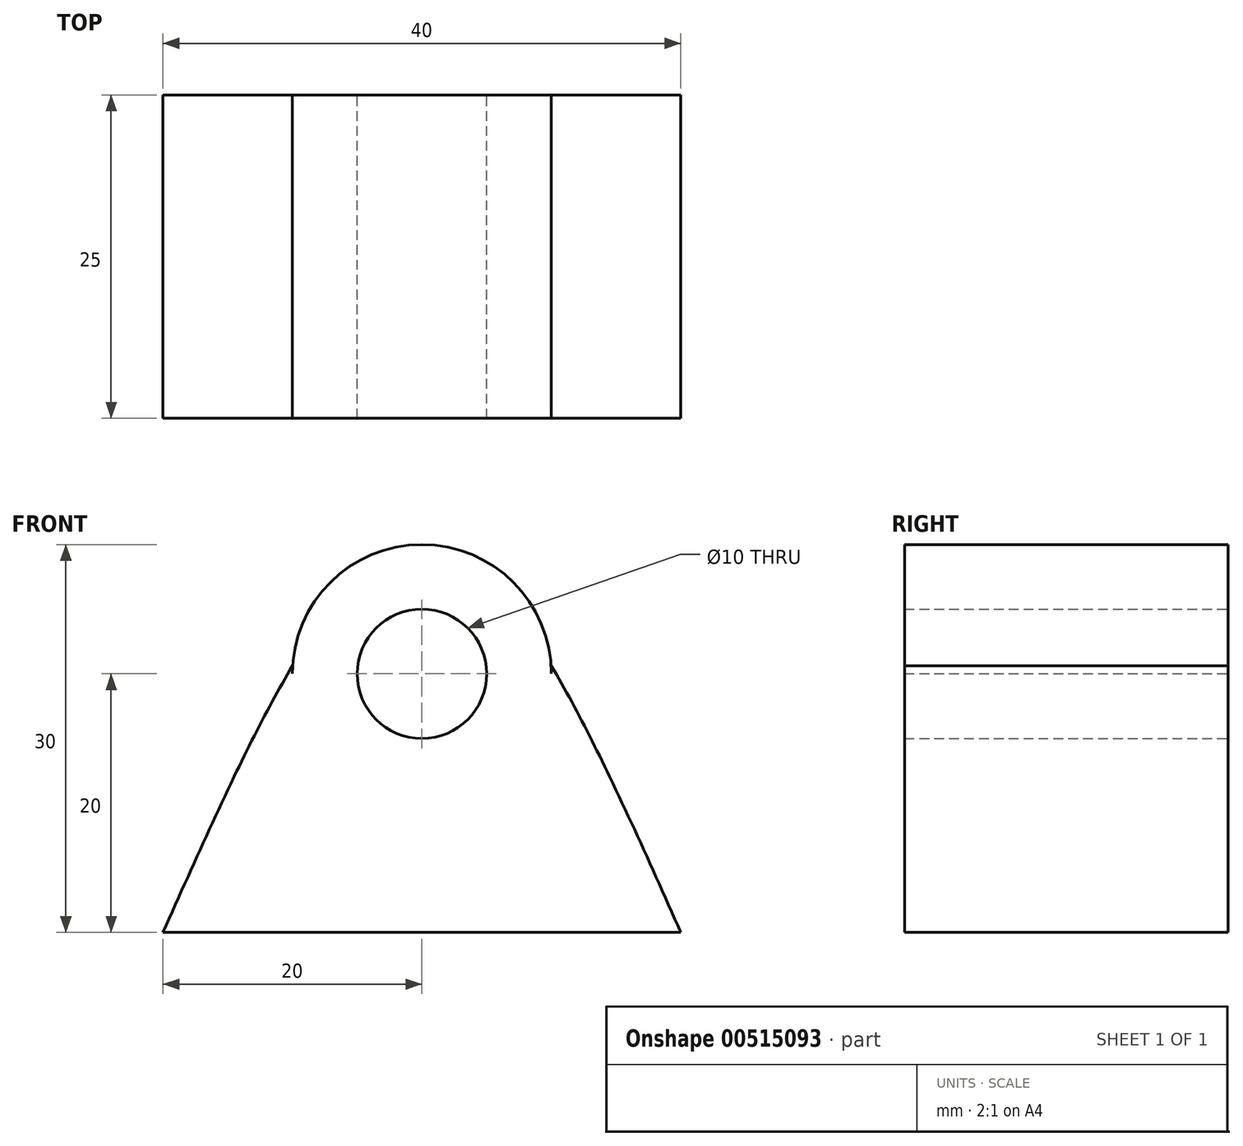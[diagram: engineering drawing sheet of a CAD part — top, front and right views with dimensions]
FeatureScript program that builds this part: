
annotation { "Feature Type Name" : "Feature", "Feature Type Description" : "" }
export const myFeature = defineFeature(function(context is Context, id is Id, definition is map)
    precondition{}
    {
        {
            var Q0;
            Q0=qCreatedBy(makeId("Front.planeOp"),FACE);
            var sketch = newSketch(context, id + "F0", { "sketchPlane" : qUnion([Q0])});
            skCircle(sketch, "E0", {"center": v(0, 20) * mm, "radius": 5 * mm});
            skSolve(sketch);
        }
        {
            var Q0;
            Q0=qCreatedBy(makeId("Front.planeOp"),FACE);
            var sketch = newSketch(context, id + "F1", { "sketchPlane" : qUnion([Q0])});
            skLineSegment(sketch, "E1.bottom", {"start": v(10, 0) * mm, "end": v(-10, 0) * mm});
            skLineSegment(sketch, "E1.top", {"start": v(10, 30) * mm, "end": v(-10, 30) * mm});
            skLineSegment(sketch, "E1.left", {"start": v(10, 0) * mm, "end": v(10, 30) * mm});
            skLineSegment(sketch, "E1.right", {"start": v(-10, 0) * mm, "end": v(-10, 30) * mm});
            skCircle(sketch, "E2", {"center": v(0, 20) * mm, "radius": 10 * mm});
            skLineSegment(sketch, "E3.bottom", {"start": v(-20, 12.04) * mm, "end": v(20, 12.04) * mm});
            skLineSegment(sketch, "E3.top", {"start": v(-20, 0) * mm, "end": v(20, 0) * mm});
            skLineSegment(sketch, "E3.left", {"start": v(-20, 12.04) * mm, "end": v(-20, 0) * mm});
            skLineSegment(sketch, "E3.right", {"start": v(20, 12.04) * mm, "end": v(20, 0) * mm});
            skFitSpline(sketch, "E4", {"points": [v(-20, 0) * mm, v(0, 30) * mm, v(20, 0) * mm], "startDerivative": vector(40, 90) * mm, "endDerivative": vector(40, -90) * mm});
            skSolve(sketch);
        }
        {
            var Q0;
            {var subQ0=sQuery(id+"F1.wireOp",EDGE,"E2");var subQ1=makeQuery(id+"F1.imprint","INTERSECT",VERTEX,{"derivedFrom":[sQuery(id+"F1.wireOp",EDGE,"E1.left"),subQ0]});Q0=makeQuery(id+"F1.imprint","IMPRINT",FACE,{"disambiguationData":[TD([[makeQuery(id+"F1.imprint","IMPRINT",EDGE,{"disambiguationData":[TD([[subQ1,-1.0]])],"derivedFrom":subQ0}),1.0]])]});}
            var Q1;
            {var subQ0=sQuery(id+"F1.wireOp",EDGE,"E3.bottom");var subQ1=sQuery(id+"F1.wireOp",EDGE,"E1.right");var subQ2=makeQuery(id+"F1.imprint","INTERSECT",VERTEX,{"derivedFrom":[subQ1,subQ0]});Q1=makeQuery(id+"F1.imprint","IMPRINT",FACE,{"disambiguationData":[TD([[makeQuery(id+"F1.imprint","IMPRINT",EDGE,{"disambiguationData":[TD([[subQ2,-1.0]])],"derivedFrom":subQ1}),-1.0]])]});}
            var Q2;
            {var subQ0=sQuery(id+"F1.wireOp",EDGE,"E3.bottom");var subQ1=sQuery(id+"F1.wireOp",EDGE,"E1.right");var subQ2=makeQuery(id+"F1.imprint","INTERSECT",VERTEX,{"derivedFrom":[subQ1,subQ0]});Q2=makeQuery(id+"F1.imprint","IMPRINT",FACE,{"disambiguationData":[TD([[makeQuery(id+"F1.imprint","IMPRINT",EDGE,{"disambiguationData":[TD([[subQ2,-1.0]])],"derivedFrom":subQ1}),1.0]])]});}
            var Q3;
            {var subQ0=sQuery(id+"F1.wireOp",EDGE,"E3.top");var subQ1=sQuery(id+"F1.wireOp",EDGE,"E1.right");var subQ2=makeQuery(id+"F1.imprint","INTERSECT",VERTEX,{"derivedFrom":[subQ1,subQ0]});Q3=makeQuery(id+"F1.imprint","IMPRINT",FACE,{"disambiguationData":[TD([[makeQuery(id+"F1.imprint","IMPRINT",EDGE,{"disambiguationData":[TD([[subQ2,-1.0]])],"derivedFrom":subQ1}),1.0]])]});}
            var Q4;
            {var subQ6=sQuery(id+"F1.wireOp",EDGE,"E3.top");var subQ8=sQuery(id+"F1.wireOp",EDGE,"E1.left");var subQ9=makeQuery(id+"F1.imprint","INTERSECT",VERTEX,{"derivedFrom":[subQ8,subQ6]});Q4=makeQuery(id+"F1.imprint","IMPRINT",FACE,{"disambiguationData":[TD([[makeQuery(id+"F1.imprint","IMPRINT",EDGE,{"disambiguationData":[TD([[subQ9,-1.0]])],"derivedFrom":subQ8}),1.0]])]});}
            var Q5;
            {var subQ0=sQuery(id+"F1.wireOp",EDGE,"E3.bottom");var subQ1=sQuery(id+"F1.wireOp",EDGE,"E1.left");var subQ2=makeQuery(id+"F1.imprint","INTERSECT",VERTEX,{"derivedFrom":[subQ1,subQ0]});Q5=makeQuery(id+"F1.imprint","IMPRINT",FACE,{"disambiguationData":[TD([[makeQuery(id+"F1.imprint","IMPRINT",EDGE,{"disambiguationData":[TD([[subQ2,-1.0]])],"derivedFrom":subQ1}),1.0]])]});}
            var Q6;
            {var subQ0=sQuery(id+"F1.wireOp",EDGE,"E3.bottom");var subQ1=sQuery(id+"F1.wireOp",EDGE,"E2");var subQ2=makeQuery(id+"F1.imprint","INTERSECT",VERTEX,{"disambiguationData":[OD(0.0)],"derivedFrom":[subQ1,subQ0]});Q6=makeQuery(id+"F1.imprint","IMPRINT",FACE,{"disambiguationData":[TD([[makeQuery(id+"F1.imprint","IMPRINT",EDGE,{"disambiguationData":[TD([[subQ2,-1.0]])],"derivedFrom":subQ1}),1.0]])]});}
            var Q7;
            {var subQ0=sQuery(id+"F1.wireOp",EDGE,"E3.bottom");var subQ1=sQuery(id+"F1.wireOp",EDGE,"E1.left");var subQ2=makeQuery(id+"F1.imprint","INTERSECT",VERTEX,{"derivedFrom":[subQ1,subQ0]});Q7=makeQuery(id+"F1.imprint","IMPRINT",FACE,{"disambiguationData":[TD([[makeQuery(id+"F1.imprint","IMPRINT",EDGE,{"disambiguationData":[TD([[subQ2,-1.0]])],"derivedFrom":subQ1}),-1.0]])]});}
            var Q8;
            {var subQ0=sQuery(id+"F1.wireOp",EDGE,"E3.top");var subQ1=sQuery(id+"F1.wireOp",EDGE,"E1.left");var subQ2=makeQuery(id+"F1.imprint","INTERSECT",VERTEX,{"derivedFrom":[subQ1,subQ0]});Q8=makeQuery(id+"F1.imprint","IMPRINT",FACE,{"disambiguationData":[TD([[makeQuery(id+"F1.imprint","IMPRINT",EDGE,{"disambiguationData":[TD([[subQ2,-1.0]])],"derivedFrom":subQ1}),-1.0]])]});}
            var Q9;
            {var subQ0=sQuery(id+"F1.wireOp",EDGE,"E4");var subQ1=sQuery(id+"F1.wireOp",EDGE,"E2");var subQ2=makeQuery(id+"F1.imprint","INTERSECT",VERTEX,{"disambiguationData":[OD(0.0)],"derivedFrom":[subQ1,subQ0]});Q9=makeQuery(id+"F1.imprint","IMPRINT",FACE,{"disambiguationData":[TD([[makeQuery(id+"F1.imprint","IMPRINT",EDGE,{"disambiguationData":[TD([[subQ2,-1.0]])],"derivedFrom":subQ1}),1.0]])]});}
            var Q10;
            {var subQ0=sQuery(id+"F1.wireOp",EDGE,"E4");var subQ1=sQuery(id+"F1.wireOp",EDGE,"E2");var subQ2=makeQuery(id+"F1.imprint","INTERSECT",VERTEX,{"disambiguationData":[OD(1.0)],"derivedFrom":[subQ1,subQ0]});Q10=makeQuery(id+"F1.imprint","IMPRINT",FACE,{"disambiguationData":[TD([[makeQuery(id+"F1.imprint","IMPRINT",EDGE,{"disambiguationData":[TD([[subQ2,1.0]])],"derivedFrom":subQ1}),1.0]])]});}
            extrude(context, id + "F2", {"entities" : qUnion([Q0, Q1, Q2, Q3, Q4, Q5, Q6, Q7, Q8, Q9, Q10]), "endBound" : BoundingType.SYMMETRIC, "depth" : 25 * mm, "offsetDistance" : 25.4 * mm});
        }
        {
            var Q0;
            Q0=makeQuery(id+"F0.imprint","IMPRINT",FACE,{"disambiguationData":[TD([[makeQuery(id+"F0.imprint","IMPRINT",EDGE,{"derivedFrom":sQuery(id+"F0.wireOp",EDGE,"E0")}),1.0]])]});
            extrude(context, id + "F3", {"entities" : qUnion([Q0]), "operationType" : NewBodyOperationType.REMOVE, "endBound" : BoundingType.SYMMETRIC, "depth" : 25 * mm, "offsetDistance" : 25.4 * mm});
        }
    });
